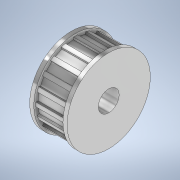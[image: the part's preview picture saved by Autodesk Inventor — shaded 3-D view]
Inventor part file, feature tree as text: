
AUTODESK INVENTOR PART (.ipt)
format: ipt  version: 2021 (Build 250183000, 183)  size: 232,448 bytes
history: native  units: mm
features: extrude x4, sketch x4, plane x1
ambient origin geometry x8: Origin, YZ Plane, XZ Plane, XY Plane, X Axis, Y Axis, Z Axis, Center Point
bodies: Solid1 (feature_tree)
feature tree (9):
  extrude  "Extrusion1"  Depth=9.0mm TaperAngle=0.0deg
  extrude  "Extrusion2"  Depth=9.0mm TaperAngle=0.0deg
  plane  "Work Plane2"
  extrude  "Extrusion3"  Depth=18.0mm
  extrude  "Extrusion4"  Depth=1.0mm
  sketch  "Sketch1"  dims[d0=20.0mm d1=9.0mm d2=0.0mm]
  sketch  "Sketch2"  dims[d3=5.0mm d4=9.0mm d5=0.0mm]
  sketch  "Sketch3"  dims[d6=-1.0mm d7=18.0mm]
  sketch  "Sketch4"  dims[d8=7.0mm d9=0.0mm d10=1.0mm d11=1.0mm d13=200.0mm d15=360.0deg d17=7.0mm d18=0.0mm]
